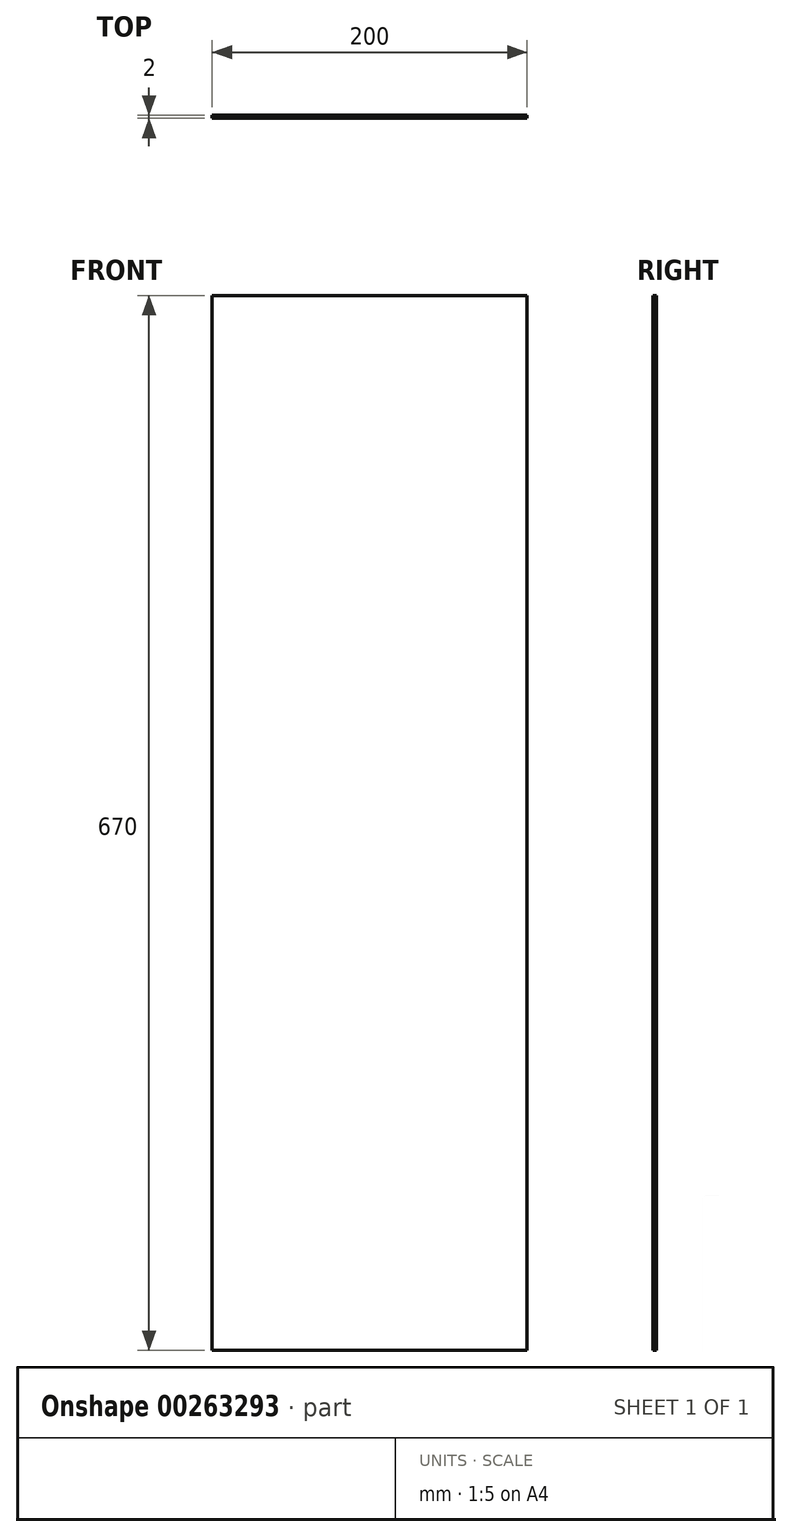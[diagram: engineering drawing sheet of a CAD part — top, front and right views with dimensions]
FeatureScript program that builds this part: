
annotation { "Feature Type Name" : "Feature", "Feature Type Description" : "" }
export const myFeature = defineFeature(function(context is Context, id is Id, definition is map)
    precondition{}
    {
        {
            var Q0;
            Q0=qCreatedBy(makeId("Front.planeOp"),FACE);
            var sketch = newSketch(context, id + "F0", { "sketchPlane" : qUnion([Q0])});
            skLineSegment(sketch, "E0.bottom", {"start": v(100, -335) * mm, "end": v(-100, -335) * mm});
            skLineSegment(sketch, "E0.top", {"start": v(100, 335) * mm, "end": v(-100, 335) * mm});
            skLineSegment(sketch, "E0.left", {"start": v(100, -335) * mm, "end": v(100, 335) * mm});
            skLineSegment(sketch, "E0.right", {"start": v(-100, -335) * mm, "end": v(-100, 335) * mm});
            skPoint(sketch, "E0.middle", {"position": v(0, 0) * mm});
            skSolve(sketch);
        }
        {
            var Q0;
            Q0 = qSketchRegion(id + "F0", true);
            extrude(context, id + "F1", {"entities" : qUnion([Q0]), "depth" : 2 * mm});
        }
    });
